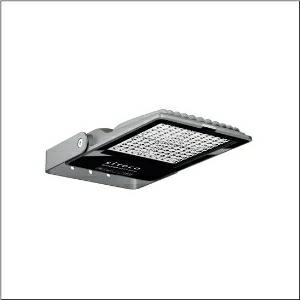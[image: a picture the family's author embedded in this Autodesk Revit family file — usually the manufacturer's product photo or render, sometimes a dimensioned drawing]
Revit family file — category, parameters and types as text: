
# Revit family: sicompact_r__31_mini___pl32_5xa7571c2k23_606d
name_source: partatom
category: Lighting Fixtures
units: mm (PartAtom-declared; Revit-internal decimal feet)

## family parameters
Cut with Voids When Loaded = No
Host = Face
Light Source = No
Part Type = Normal
Room Calculation Point = No
Round Connector Dimension = Use Diameter
Shared = No

## types (1)
- SiCompact® 31 mini  PL32 (1 x LED, 15000 lm, 95 W, 4000K)
    Apparent Load = 95 VA
    CIE Flux Codes = 32 69 98 100 100
    Color Rendering = 70
    Color Temperature = 4000K
    Default Elevation = 1800 mm
    Description = SiCompact® 31 mini, floodlight, primary light control with lens, of plastic, of toughened safety glass, transparent, light distribution: PL32, light emission: direct distribution, primary light characteristic: asymmetric, installation type: surface-mounted, LED, High Power LED, rated luminous flux: 15.000lm, luminous efficacy: 158lm/W, light colour: 740, colour temperature: 4000K, control gear: ON/OFF, with cable, 3x 1.5mm², mains connection: 220..240V, AC, 50/60Hz, connection cable pre-assembled, cable length: 2m, rated input power: 95W, of diecast aluminium, specular, metallic grey (RAL 9006), length: 461mm, width: 261mm, height: 62mm, bracket, of sheet steel, coated, metallic grey (RAL 9006), ON/OFF, protection rating (complete): IP66, insulation class (complete): insulation class I (protective earthing), certification: CE, ENEC, impact resistance: IK08, permissible operating ambient temperature: -40..+45°C, packaging unit: 1 piece

Light Distribution: PL32
    Height = 62 mm  [stored 0.203412 ft]
    Lamp = 1 x LED
    Lamp Light Flux = 15000 lm
    Lamp Power = 95 W
    Lamp count = 1
    Length = 460 mm
    Luminous efficacy = 158 lm/W
    Manufacturer = Siteco
    ModVariant = No
    Model = 5XA7571C2K23
    Mounting Place = Wall
    Mounting Type = Surface mounted
    Number of Poles = 1
    OnlyDefault = Yes
    Power Factor = 1
    Product Name = SiCompact® 31 mini | PL32
    Product group = floodlight | wall mounted
    ProductGroupID = 2001
    Protection Class = Protection class I
    Protection Degree = IP 66
    RLX_Detail_Level = 1
    RLX_Emergency_Light_Flux = 0 lm
    RLX_Emergency_Type = 0
    RLX_Emergency_Type_DB = No
    RlxData = <blob elided: 126733 chars, md5=47790856>
    Socket = socket
    Standby Power = 0 W
    System Light Flux = 15000 lm
    System Power = 95 W
    Type Comments = Product without accessories
    Type Image = l_1006951.jpg
    URL = http://relux.com
    VarID = ---
    Voltage = 0 V
    Weight = 0.00 kg
    Width = 260 mm

note: [stored X ft] marks values corroborated as IEEE doubles in the binary element streams (Revit-internal decimal feet)

## geometry (parser evidence)
native form markers: Blend x4, Sweep x12
no freeform markers — native parametric forms only
